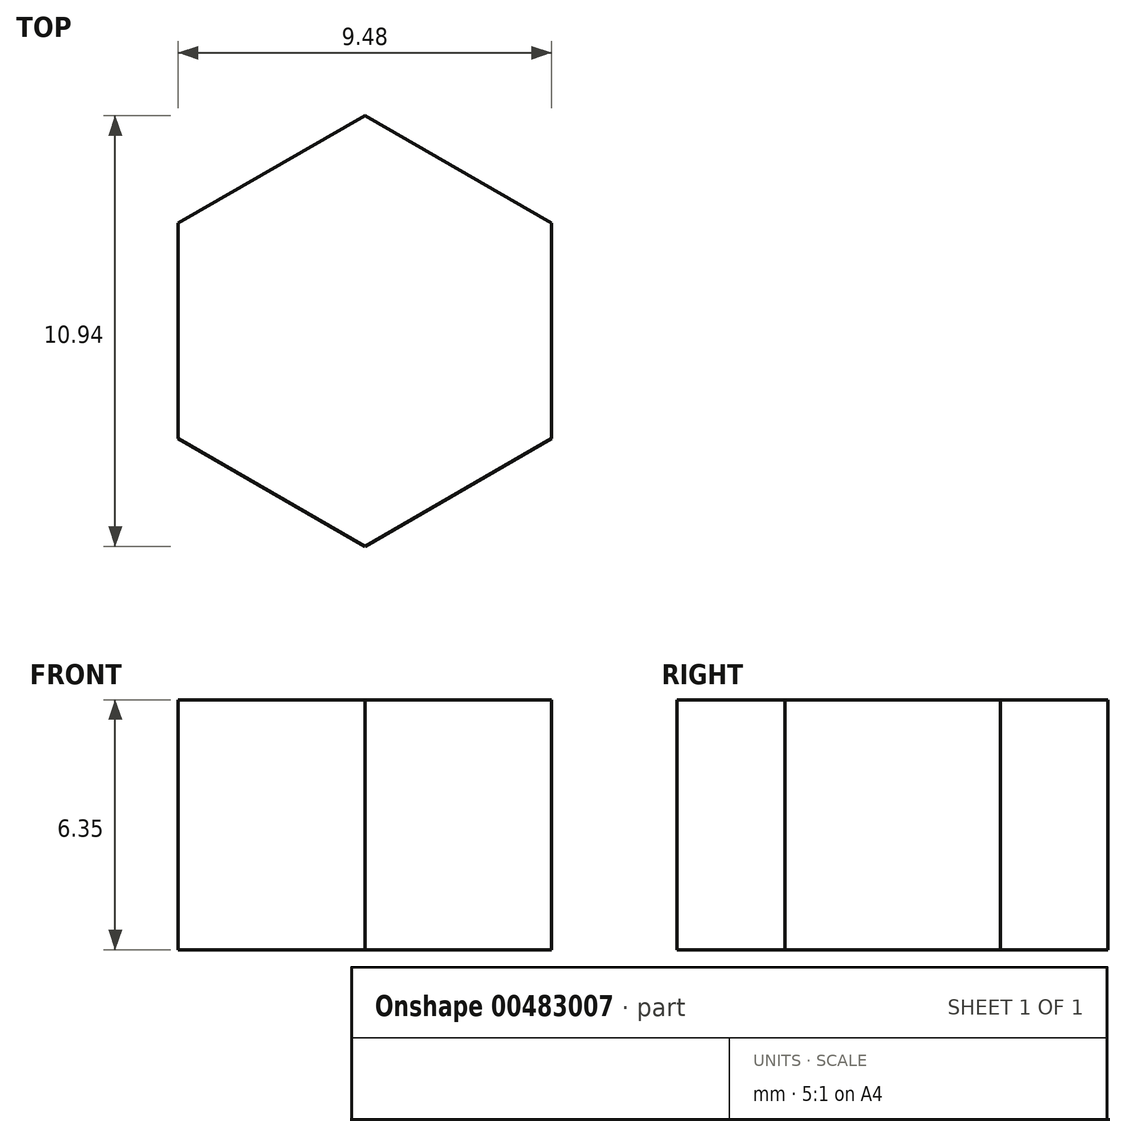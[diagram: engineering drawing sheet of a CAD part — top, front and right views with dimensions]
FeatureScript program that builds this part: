
annotation { "Feature Type Name" : "Feature", "Feature Type Description" : "" }
export const myFeature = defineFeature(function(context is Context, id is Id, definition is map)
    precondition{}
    {
        {
            var Q0;
            Q0=qCreatedBy(makeId("Top.planeOp"),FACE);
            var sketch = newSketch(context, id + "F0", { "sketchPlane" : qUnion([Q0])});
            skCircle(sketch, "E0.cCircle", {"center": v(0, 0) * mm, "radius": 5.47 * mm, "construction": true});
            skLineSegment(sketch, "E0.0", {"start": v(4.74, -2.74) * mm, "end": v(0, -5.47) * mm});
            skLineSegment(sketch, "E0.1", {"start": v(0, -5.47) * mm, "end": v(-4.74, -2.74) * mm});
            skLineSegment(sketch, "E0.2", {"start": v(-4.74, -2.74) * mm, "end": v(-4.74, 2.74) * mm});
            skLineSegment(sketch, "E0.3", {"start": v(-4.74, 2.74) * mm, "end": v(0, 5.47) * mm});
            skLineSegment(sketch, "E0.4", {"start": v(0, 5.47) * mm, "end": v(4.74, 2.74) * mm});
            skLineSegment(sketch, "E0.5", {"start": v(4.74, 2.74) * mm, "end": v(4.74, -2.74) * mm});
            skSolve(sketch);
        }
        {
            var Q0;
            Q0=makeQuery(id+"F0.imprint","IMPRINT",FACE,{"disambiguationData":[TD([[makeQuery(id+"F0.imprint","IMPRINT",EDGE,{"derivedFrom":sQuery(id+"F0.wireOp",EDGE,"E0.0")}),-1.0]])]});
            var Q1;
            Q1=makeQuery(id+"F0.imprint","IMPRINT",FACE,{"disambiguationData":[TD([[makeQuery(id+"F0.imprint","IMPRINT",EDGE,{"derivedFrom":sQuery(id+"F0.wireOp",EDGE,"d9cd2016-d458-4e4d-9cf3-df2efdb492b5.0")}),-1.0]])]});
            var Q2;
            Q2=makeQuery(id+"F0.imprint","IMPRINT",FACE,{"disambiguationData":[TD([[makeQuery(id+"F0.imprint","IMPRINT",EDGE,{"derivedFrom":sQuery(id+"F0.wireOp",EDGE,"KNA0DRVw-JIxy-f3xc-Q7Qd-CCeJbsmVBZYs")}),1.0]])]});
            extrude(context, id + "F1", {"entities" : qUnion([Q0, Q1, Q2]), "depth" : 6.35 * mm});
        }
    });
